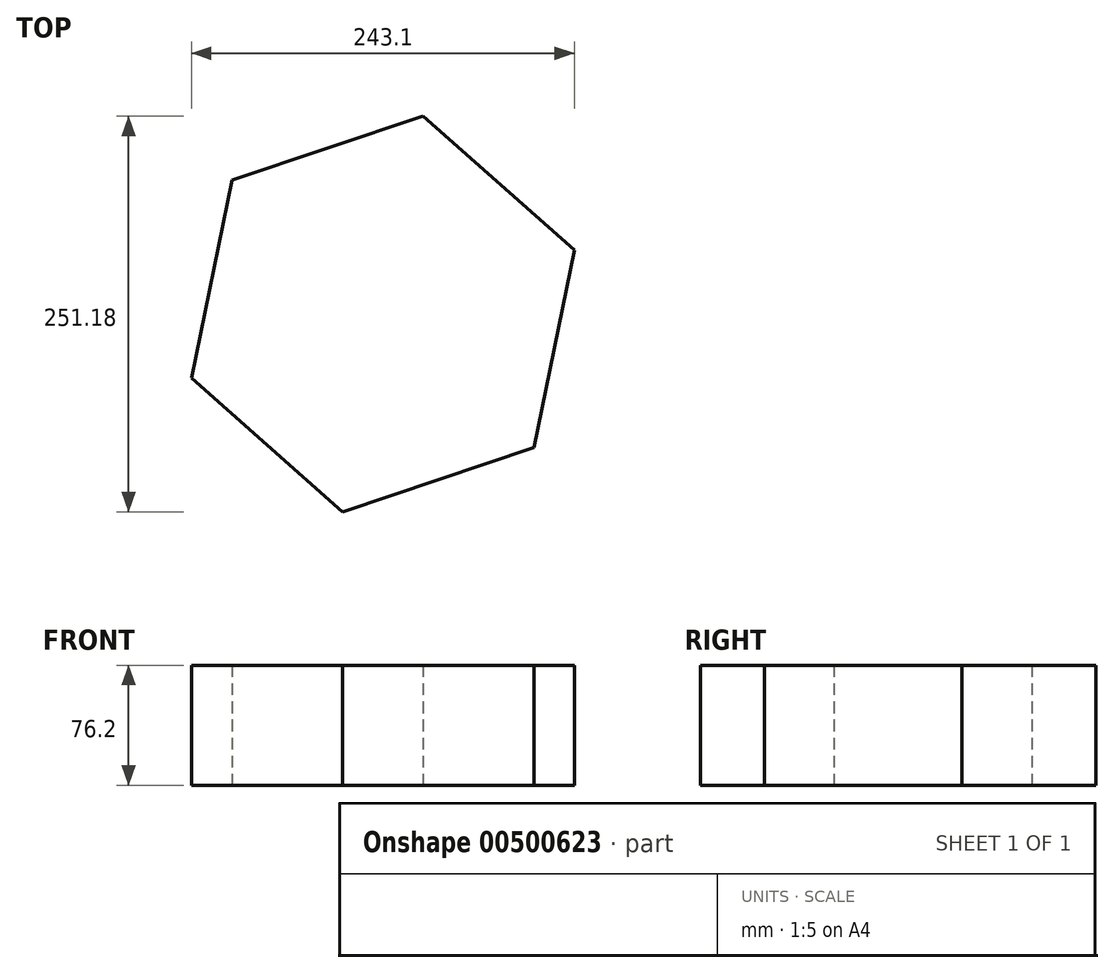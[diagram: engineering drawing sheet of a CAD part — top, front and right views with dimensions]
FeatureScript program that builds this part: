
annotation { "Feature Type Name" : "Feature", "Feature Type Description" : "" }
export const myFeature = defineFeature(function(context is Context, id is Id, definition is map)
    precondition{}
    {
        {
            var Q0;
            Q0=qCreatedBy(makeId("Top.planeOp"),FACE);
            var sketch = newSketch(context, id + "F0", { "sketchPlane" : qUnion([Q0])});
            skCircle(sketch, "E0.cCircle", {"center": v(0, 0) * mm, "radius": 128.17 * mm, "construction": true});
            skLineSegment(sketch, "E0.0", {"start": v(121.55, 40.66) * mm, "end": v(95.99, -84.93) * mm});
            skLineSegment(sketch, "E0.1", {"start": v(95.99, -84.93) * mm, "end": v(-25.56, -125.6) * mm});
            skLineSegment(sketch, "E0.2", {"start": v(-25.56, -125.6) * mm, "end": v(-121.55, -40.66) * mm});
            skLineSegment(sketch, "E0.3", {"start": v(-121.55, -40.66) * mm, "end": v(-95.99, 84.93) * mm});
            skLineSegment(sketch, "E0.4", {"start": v(-95.99, 84.93) * mm, "end": v(25.56, 125.6) * mm});
            skLineSegment(sketch, "E0.5", {"start": v(25.56, 125.6) * mm, "end": v(121.55, 40.66) * mm});
            skSolve(sketch);
        }
        {
            var Q0;
            Q0=makeQuery(id+"F0.imprint","IMPRINT",FACE,{"disambiguationData":[TD([[makeQuery(id+"F0.imprint","IMPRINT",EDGE,{"derivedFrom":sQuery(id+"F0.wireOp",EDGE,"E0.0")}),-1.0]])]});
            extrude(context, id + "F1", {"entities" : qUnion([Q0]), "depth" : 76.2 * mm});
        }
    });
